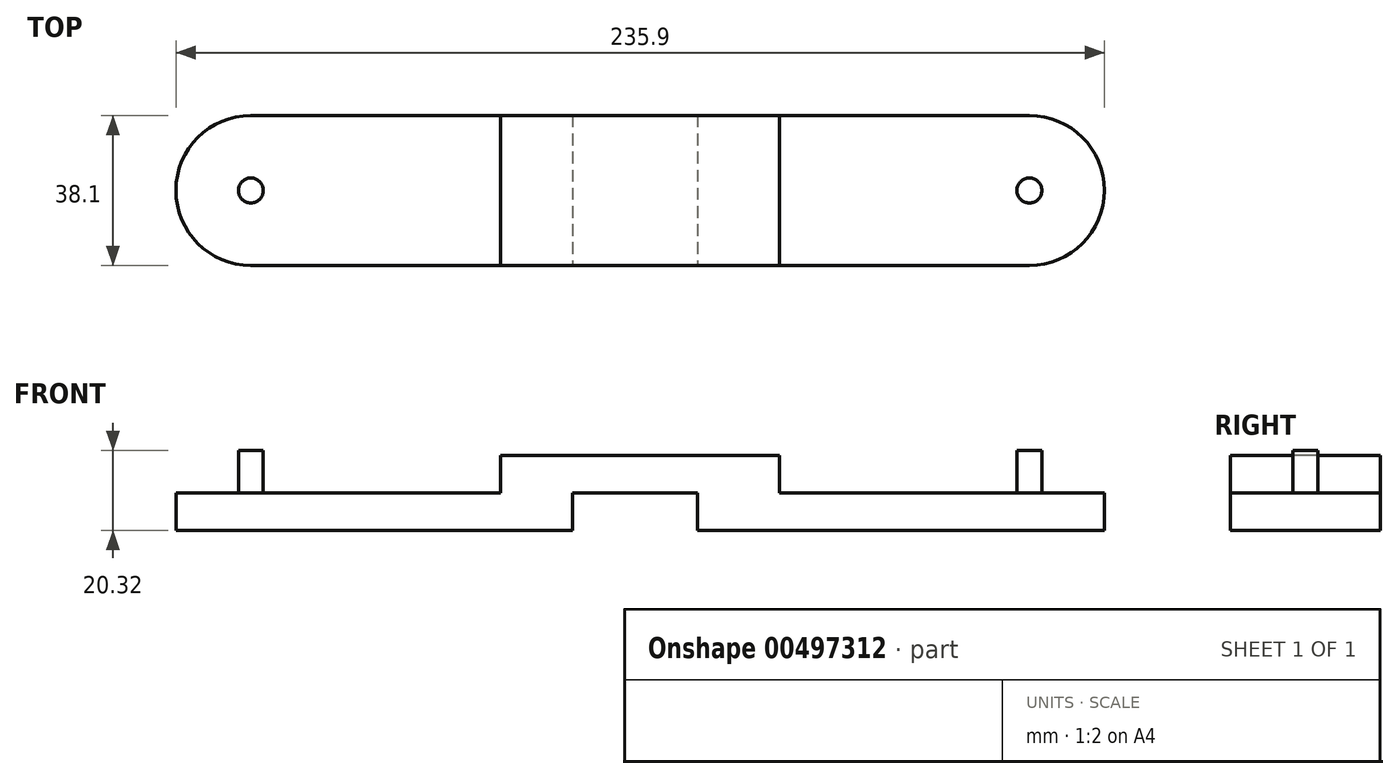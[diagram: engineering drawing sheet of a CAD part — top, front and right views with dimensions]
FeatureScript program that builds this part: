
annotation { "Feature Type Name" : "Feature", "Feature Type Description" : "" }
export const myFeature = defineFeature(function(context is Context, id is Id, definition is map)
    precondition{}
    {
        {
            var Q0;
            Q0=qCreatedBy(makeId("Top.planeOp"),FACE);
            var sketch = newSketch(context, id + "F0", { "sketchPlane" : qUnion([Q0])});
            skLineSegment(sketch, "E0", {"start": v(-97.64, 19.6) * mm, "end": v(100.16, 19.6) * mm, "construction": true});
            skCircle(sketch, "E1", {"center": v(-97.64, 19.6) * mm, "radius": 3.18 * mm});
            skCircle(sketch, "E2", {"center": v(100.16, 19.6) * mm, "radius": 3.18 * mm});
            skLineSegment(sketch, "E3", {"start": v(100.16, 38.66) * mm, "end": v(-97.64, 38.66) * mm});
            skLineSegment(sketch, "E4", {"start": v(100.16, 0.56) * mm, "end": v(-97.64, 0.56) * mm});
            skArc(sketch, "E5", {"start": v(-97.64, 38.66) * mm, "mid": v(-116.7, 19.6) * mm, "end": v(-97.64, 0.56) * mm});
            skArc(sketch, "E6", {"start": v(100.16, 38.66) * mm, "mid": v(119.2, 19.6) * mm, "end": v(100.16, 0.56) * mm});
            skSolve(sketch);
        }
        {
            var Q0;
            Q0 = qSketchRegion(id + "F0", true);
            extrude(context, id + "F1", {"entities" : qUnion([Q0]), "depth" : 19.05 * mm});
        }
        {
            var Q0;
            Q0=makeQuery(id+"F1.opExtrude","CAP_FACE",FACE,{"disambiguationData":[OSD([sQuery(id+"F0.wireOp",EDGE,"E1"),sQuery(id+"F0.wireOp",EDGE,"E2"),sQuery(id+"F0.wireOp",EDGE,"UDonizd9-KIUs-aUjc-FvjQ-oS9ooLD7nvKp"),sQuery(id+"F0.wireOp",EDGE,"fdub3FZR-vsTT-j1jE-QnHJ-qFB0he3KxKwz"),sQuery(id+"F0.wireOp",EDGE,"E3"),sQuery(id+"F0.wireOp",EDGE,"E4")])],"isStart":false});
            var sketch = newSketch(context, id + "F2", { "sketchPlane" : qUnion([Q0])});
            skLineSegment(sketch, "E7.0", {"start": v(100.15, 45) * mm, "end": v(36.65, 45) * mm});
            skLineSegment(sketch, "E8.MirrorCS", {"start": v(100.15, -5.8) * mm, "end": v(36.65, -5.8) * mm});
            skLineSegment(sketch, "E9", {"start": v(-34.14, 45) * mm, "end": v(-34.14, -5.8) * mm});
            skLineSegment(sketch, "E10", {"start": v(36.65, 45) * mm, "end": v(36.65, -5.8) * mm});
            skLineSegment(sketch, "E11.trimOffspring", {"start": v(-34.14, 45) * mm, "end": v(-97.64, 45) * mm});
            skLineSegment(sketch, "E12.trimOffspring", {"start": v(-34.14, -5.8) * mm, "end": v(-97.64, -5.8) * mm});
            skLineSegment(sketch, "E13", {"start": v(100.15, 19.6) * mm, "end": v(-97.64, 19.6) * mm, "construction": true});
            skArc(sketch, "E14", {"start": v(-97.64, 45) * mm, "mid": v(-123.04, 19.6) * mm, "end": v(-97.64, -5.8) * mm});
            skArc(sketch, "E15", {"start": v(100.15, 45) * mm, "mid": v(125.55, 19.6) * mm, "end": v(100.15, -5.8) * mm});
            skSolve(sketch);
        }
        {
            var Q0;
            Q0=makeQuery(id+"F2.imprint","IMPRINT",FACE,{"disambiguationData":[TD([[makeQuery(id+"F2.imprint","IMPRINT",EDGE,{"derivedFrom":makeQuery(id+"F1.opExtrude","CAP_EDGE",EDGE,{"disambiguationData":[OSD([sQuery(id+"F0.wireOp",EDGE,"E1")])],"isStart":false})}),1.0]])]});
            var Q1;
            Q1=makeQuery(id+"F2.imprint","IMPRINT",FACE,{"disambiguationData":[TD([[makeQuery(id+"F2.imprint","IMPRINT",EDGE,{"derivedFrom":makeQuery(id+"F1.opExtrude","CAP_EDGE",EDGE,{"disambiguationData":[OSD([sQuery(id+"F0.wireOp",EDGE,"E2")])],"isStart":false})}),1.0]])]});
            var Q2;
            {var subQ1=sQuery(id+"F2.wireOp",EDGE,"E7.0");Q2=makeQuery(id+"F2.imprint","IMPRINT",FACE,{"disambiguationData":[TD([[makeQuery(id+"F2.imprint","IMPRINT",EDGE,{"derivedFrom":subQ1}),1.0]])]});}
            var Q3;
            Q3=makeQuery(id+"F2.imprint","IMPRINT",FACE,{"disambiguationData":[TD([[makeQuery(id+"F2.imprint","IMPRINT",EDGE,{"derivedFrom":makeQuery(id+"F1.opExtrude","CAP_EDGE",EDGE,{"disambiguationData":[OSD([sQuery(id+"F0.wireOp",EDGE,"E1")])],"isStart":false})}),-1.0]])]});
            var Q4;
            Q4=makeQuery(id+"F2.imprint","IMPRINT",FACE,{"disambiguationData":[TD([[makeQuery(id+"F2.imprint","IMPRINT",EDGE,{"derivedFrom":makeQuery(id+"F1.opExtrude","CAP_EDGE",EDGE,{"disambiguationData":[OSD([sQuery(id+"F0.wireOp",EDGE,"E2")])],"isStart":false})}),-1.0]])]});
            extrude(context, id + "F3", {"entities" : qUnion([Q0, Q1, Q2, Q3, Q4]), "operationType" : NewBodyOperationType.REMOVE, "oppositeDirection" : true, "depth" : 9.52 * mm});
        }
        {
            var Q0;
            Q0=makeQuery(id+"F1.opExtrude","CAP_FACE",FACE,{"disambiguationData":[OSD([sQuery(id+"F0.wireOp",EDGE,"E1"),sQuery(id+"F0.wireOp",EDGE,"E2"),sQuery(id+"F0.wireOp",EDGE,"UDonizd9-KIUs-aUjc-FvjQ-oS9ooLD7nvKp"),sQuery(id+"F0.wireOp",EDGE,"fdub3FZR-vsTT-j1jE-QnHJ-qFB0he3KxKwz"),sQuery(id+"F0.wireOp",EDGE,"E3"),sQuery(id+"F0.wireOp",EDGE,"E4")])],"isStart":true});
            var sketch = newSketch(context, id + "F4", { "sketchPlane" : qUnion([Q0])});
            skLineSegment(sketch, "E16", {"start": v(-97.64, -19.6) * mm, "end": v(100.16, -19.6) * mm});
            skLineSegment(sketch, "E17", {"start": v(0, -19.6) * mm, "end": v(0, -50.8) * mm});
            skLineSegment(sketch, "E18.bottom", {"start": v(15.88, -50.8) * mm, "end": v(-15.87, -50.8) * mm});
            skLineSegment(sketch, "E18.top", {"start": v(15.87, 0) * mm, "end": v(-15.87, 0) * mm});
            skLineSegment(sketch, "E18.left", {"start": v(15.87, -50.8) * mm, "end": v(15.88, 0) * mm});
            skLineSegment(sketch, "E18.right", {"start": v(-15.87, -50.8) * mm, "end": v(-15.87, 0) * mm});
            skSolve(sketch);
        }
        {
            var Q0;
            Q0 = qSketchRegion(id + "F4", true);
            extrude(context, id + "F5", {"entities" : qUnion([Q0]), "operationType" : NewBodyOperationType.REMOVE, "oppositeDirection" : true, "depth" : 9.52 * mm});
        }
        {
            var Q0;
            {var subQ0=sQuery(id+"F0.wireOp",EDGE,"E5");var subQ1=sQuery(id+"F0.wireOp",EDGE,"E3");var subQ2=sQuery(id+"F0.wireOp",EDGE,"E4");var subQ3=sQuery(id+"F0.wireOp",EDGE,"E1");Q0=makeQuery(id+"F5.boolean.opBoolean","SPLIT",FACE,{"disambiguationData":[TD([makeQuery(id+"F1.opExtrude","SWEPT_FACE",FACE,{"disambiguationData":[OSD([subQ3])]})])],"derivedFrom":makeQuery(id+"F1.opExtrude","CAP_FACE",FACE,{"disambiguationData":[OSD([subQ3,sQuery(id+"F0.wireOp",EDGE,"E2"),subQ1,subQ2,subQ0,sQuery(id+"F0.wireOp",EDGE,"E6")])],"isStart":true})});}
            var sketch = newSketch(context, id + "F6", { "sketchPlane" : qUnion([Q0])});
            skCircle(sketch, "E19", {"center": v(-97.64, -19.6) * mm, "radius": 3.18 * mm});
            skSolve(sketch);
        }
        {
            var Q0;
            Q0=makeQuery(id+"F6.imprint","IMPRINT",FACE,{"disambiguationData":[TD([[makeQuery(id+"F6.imprint","IMPRINT",EDGE,{"derivedFrom":sQuery(id+"F6.wireOp",EDGE,"E19")}),-1.0]])]});
            extrude(context, id + "F7", {"entities" : qUnion([Q0]), "operationType" : NewBodyOperationType.ADD, "oppositeDirection" : true, "depth" : 20.32 * mm});
        }
        {
            var Q0;
            {var subQ0=sQuery(id+"F0.wireOp",EDGE,"E6");var subQ1=sQuery(id+"F0.wireOp",EDGE,"E4");var subQ2=sQuery(id+"F0.wireOp",EDGE,"E3");var subQ3=sQuery(id+"F0.wireOp",EDGE,"E2");Q0=makeQuery(id+"F5.boolean.opBoolean","SPLIT",FACE,{"disambiguationData":[TD([makeQuery(id+"F1.opExtrude","SWEPT_FACE",FACE,{"disambiguationData":[OSD([subQ3])]})])],"derivedFrom":makeQuery(id+"F1.opExtrude","CAP_FACE",FACE,{"disambiguationData":[OSD([sQuery(id+"F0.wireOp",EDGE,"E1"),subQ3,subQ2,subQ1,sQuery(id+"F0.wireOp",EDGE,"E5"),subQ0])],"isStart":true})});}
            var sketch = newSketch(context, id + "F8", { "sketchPlane" : qUnion([Q0])});
            skCircle(sketch, "E20", {"center": v(100.16, -19.6) * mm, "radius": 3.18 * mm});
            skSolve(sketch);
        }
        {
            var Q0;
            Q0=makeQuery(id+"F8.imprint","IMPRINT",FACE,{"disambiguationData":[TD([[makeQuery(id+"F8.imprint","IMPRINT",EDGE,{"derivedFrom":sQuery(id+"F8.wireOp",EDGE,"E20")}),-1.0]])]});
            extrude(context, id + "F9", {"entities" : qUnion([Q0]), "operationType" : NewBodyOperationType.ADD, "oppositeDirection" : true, "depth" : 20.32 * mm});
        }
    });
